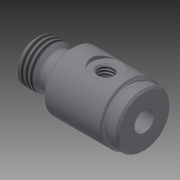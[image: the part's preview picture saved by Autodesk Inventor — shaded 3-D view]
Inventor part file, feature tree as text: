
AUTODESK INVENTOR PART (.ipt)
format: ipt  version: 2014 (Build 180170000, 170)  size: 245,760 bytes
history: native  units: in
note: dims shown in document units (in); Inventor stores cm internally (conversion verified against a paired STEP export)
features: other x84, sketch x5, revolve x4, thread x2, hole x1
ambient origin geometry x8: Origin, YZ Plane, XZ Plane, XY Plane, X Axis, Y Axis, Z Axis, Center Point
bodies: Solid1 (feature_tree)
feature tree (96):
  revolve  "Revolution1"  [1 undecoded]
  thread  "Thread1"  [1 undecoded]
  revolve  "Revolution2"  Angle=360.0deg
  hole  "Hole1"  [1 undecoded]
  revolve  "Revolution3"  [1 undecoded]
  thread  "Thread2"  [1 undecoded]
  revolve  "Revolution4"  [1 undecoded]
  other  "c2_XY"
  other  "c2_YZ"
  other  "c2_ZX"
  other  "c2_X"
  other  "c2_Y"
  other  "c2_Z"
  other  "c2_Center"
  other  "e2_XY"
  other  "e2_YZ"
  other  "e2_ZX"
  other  "e2_X"
  other  "e2_Y"
  other  "e2_Z"
  other  "e2_Center"
  other  "f1_XY"
  other  "f1_YZ"
  other  "f1_ZX"
  other  "f1_X"
  other  "f1_Y"
  other  "f1_Z"
  other  "f1_Center"
  other  "f2_XY"
  other  "f2_YZ"
  other  "f2_ZX"
  other  "f2_X"
  other  "f2_Y"
  other  "f2_Z"
  other  "f2_Center"
  other  "i1_XY"
  other  "i1_YZ"
  other  "i1_ZX"
  other  "i1_X"
  other  "i1_Y"
  other  "i1_Z"
  other  "i1_Center"
  other  "i2_XY"
  other  "i2_YZ"
  other  "i2_ZX"
  other  "i2_X"
  other  "i2_Y"
  other  "i2_Z"
  other  "i2_Center"
  other  "l1_XY"
  other  "l1_YZ"
  other  "l1_ZX"
  other  "l1_X"
  other  "l1_Y"
  other  "l1_Z"
  other  "l1_Center"
  other  "l2_XY"
  other  "l2_YZ"
  other  "l2_ZX"
  other  "l2_X"
  other  "l2_Y"
  other  "l2_Z"
  other  "l2_Center"
  other  "rod_guide_XY"
  other  "rod_guide_YZ"
  other  "rod_guide_ZX"
  other  "rod_guide_X"
  other  "rod_guide_Y"
  other  "rod_guide_Z"
  other  "rod_guide_Center"
  other  "to_mounting_bracket_XY"
  other  "to_mounting_bracket_YZ"
  other  "to_mounting_bracket_ZX"
  other  "to_mounting_bracket_X"
  other  "to_mounting_bracket_Y"
  other  "to_mounting_bracket_Z"
  other  "to_mounting_bracket_Center"
  other  "to_rod_XY"
  other  "to_rod_YZ"
  other  "to_rod_ZX"
  other  "to_rod_X"
  other  "to_rod_Y"
  other  "to_rod_Z"
  other  "to_rod_Center"
  other  "to_tube_XY"
  other  "to_tube_YZ"
  other  "to_tube_ZX"
  other  "to_tube_X"
  other  "to_tube_Y"
  other  "to_tube_Z"
  other  "to_tube_Center"
  sketch  "Sketch_2"  dims[d0=360.0deg d1=0.1557in d2=0.0in d3=360.0deg]
  sketch  "Sketch_3"  dims[d4=0.21in d5=0.75in d6=0.25in d7=0.25in d8=90.0deg d9=1.156in d10=0.0in d11=360.0deg]
  sketch  "Sketch3"  dims[d12=0.0955in d13=0.1018in d14=360.0deg]
  sketch  "Sketch_13"
  sketch  "Sketch_47"
note: 6 required parameter values undecoded (feature->parameter linkage not recoverable at this tier; creation-order binding heuristic only, values carry confidence <= 0.55)